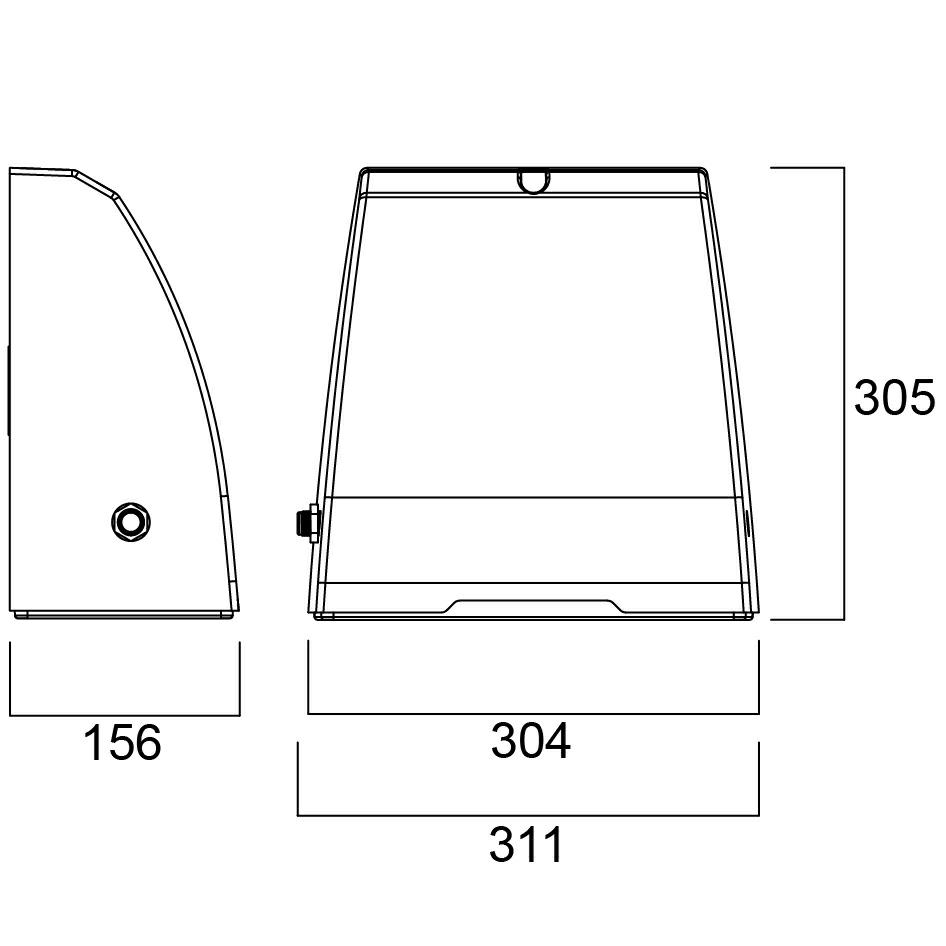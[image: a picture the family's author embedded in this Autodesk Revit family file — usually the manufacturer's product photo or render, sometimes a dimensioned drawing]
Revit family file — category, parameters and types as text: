
# Revit family: 0049944_3250lm
name_source: partatom
category: Lighting Fixtures
revit_build: Autodesk Revit 2018 (Build: 20170223_1515(x64)
units: mm (PartAtom-declared; Revit-internal decimal feet)

## family parameters
Cut with Voids When Loaded = No
Host = Face
Light Source = Yes
OmniClass Number = 23.80.70.00
OmniClass Title = Lighting
Part Type = Normal
Room Calculation Point = No
Round Connector Dimension = Use Diameter
Shared = No

## types (1)
- 0049944 MURO SURF IP65 1700-3250LM 840 PH GR
    Apparent Load = 28 VA
    Assembly Code = D5020200
    AssetType = Fixed
    ClassificationName = Uniclass2015
    ClassificationValue = EF_70_80
    Color Filter = 16777215
    Cost = 0 $
    Default Elevation = 1219 mm
    Description = Muro Surface is a wall mounted fixture for exterior lighting applications. Comes with aluminium housing in RAL7016 anthracite grey colour, frosted PC diffuser, IP65, IK10, Class I, 4000K, non-dimmable multipower driver with 5 settings, 1700 / 1900 / 2750 / 3150 / 3250 lm, 14 / 16 / 24 / 27 / 28 W, up to 121 lm/W total system efficacy, switchable built in Mini photocell, CRI80, Asymmetrical beam, 119.000 hrs L70B50 lifespan, 304 x 305 x 155 mm (L x W x D) dimensions, 4.1 kg weight.
    Dimming Lamp Color Temperature Shift = <None>
    DocumentationLiterature = http://www.sylvania-lighting.com
    ElectricShockClassification = 116
    Emit Shape Visible in Rendering = No
    Emit from Circle Diameter = 610 mm
    IfcExportAs = Class I
    IfcExportType = IfcLightFixtureType
    ImpactProtectionIndex = IfcLightFixtureType
    IngressProtection = IfcLightFixtureType
    InputNominalFrequency = 4000
    InputVoltage = 0
    LampColourRenderingIndex = 16500
    LampColourTemperature = LED
    LampMacAdamStep = 80
    LampNominalLuminous = 4000 K
    LightOutputRatio = LED
    LuminaireType = 0
    ManufacturerName = 116 lm/W
    Material = Feilo Sylvania
    Material_1_SYL = <By Category>
    Material_2_SYL = <By Category>
    Material_3_SYL = <By Category>
    Material_4_SYL = <By Category>
    Model = Muro Surface IP65 1700-3250lm 840 PH Grey
    ModelNumber = 0049944
    ModelReference = Muro Surface IP65 1700-3250lm 840 PH Grey
    Name = Muro Surface IP65 1700-3250lm 840 PH Grey
    NominalDepth = 155 mm  [stored 0.50853 ft]
    NominalHeight = 305 mm  [stored 1.00066 ft]
    NominalLength = 155 mm  [stored 0.50853 ft]
    Photometric Web File = 0049944_3250lm.IES
    PowerConsumption = Lighting
    PowerFactor = 0.95
    Tilt Angle = -90.00°
    Type Image = <None>
    TypeName = Muro Surface IP65 1700-3250lm 840 PH Grey
    URL = 0.9
    Voltage = 0 V
    WarrantyDescription = http://www.sylvania-lighting.com

note: [stored X ft] marks values corroborated as IEEE doubles in the binary element streams (Revit-internal decimal feet)

## geometry (parser evidence)
native form markers: Sweep x1
no freeform markers — native parametric forms only
